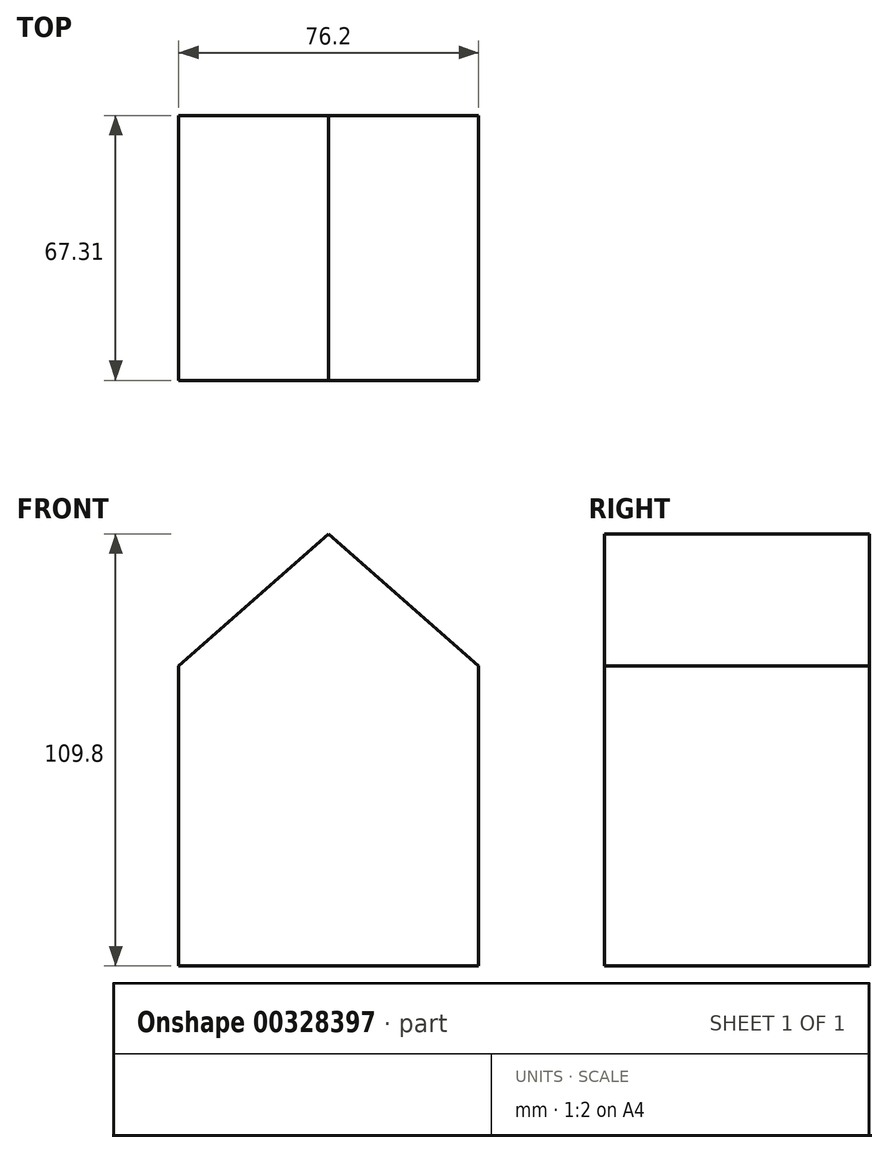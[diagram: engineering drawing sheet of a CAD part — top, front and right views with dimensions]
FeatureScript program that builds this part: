
annotation { "Feature Type Name" : "Feature", "Feature Type Description" : "" }
export const myFeature = defineFeature(function(context is Context, id is Id, definition is map)
    precondition{}
    {
        {
            var Q0;
            Q0=qCreatedBy(makeId("Front.planeOp"),FACE);
            var sketch = newSketch(context, id + "F0", { "sketchPlane" : qUnion([Q0])});
            skLineSegment(sketch, "E0.bottom", {"start": v(-38.1, 42.53) * mm, "end": v(38.1, 42.53) * mm});
            skLineSegment(sketch, "E0.top", {"start": v(-38.1, -33.67) * mm, "end": v(38.1, -33.67) * mm});
            skLineSegment(sketch, "E0.left", {"start": v(-38.1, 42.53) * mm, "end": v(-38.1, -33.67) * mm});
            skLineSegment(sketch, "E0.right", {"start": v(38.1, 42.53) * mm, "end": v(38.1, -33.67) * mm});
            skLineSegment(sketch, "E1", {"start": v(-38.1, 42.53) * mm, "end": v(0, 76.13) * mm});
            skLineSegment(sketch, "E2", {"start": v(0, 76.13) * mm, "end": v(38.1, 42.53) * mm});
            skSolve(sketch);
        }
        {
            var Q0;
            Q0=makeQuery(id+"F0.imprint","IMPRINT",FACE,{"disambiguationData":[TD([[makeQuery(id+"F0.imprint","IMPRINT",EDGE,{"derivedFrom":sQuery(id+"F0.wireOp",EDGE,"E0.bottom")}),1.0]])]});
            var Q1;
            Q1=makeQuery(id+"F0.imprint","IMPRINT",FACE,{"disambiguationData":[TD([[makeQuery(id+"F0.imprint","IMPRINT",EDGE,{"derivedFrom":sQuery(id+"F0.wireOp",EDGE,"E0.bottom")}),-1.0]])]});
            extrude(context, id + "F1", {"entities" : qUnion([Q0, Q1]), "depth" : 67.3 * mm, "offsetDistance" : 25.4 * mm});
        }
        {
            var Q0;
            Q0=makeQuery(id+"F1.opExtrude","CAP_FACE",FACE,{"disambiguationData":[OSD([sQuery(id+"F0.wireOp",EDGE,"E0.top"),sQuery(id+"F0.wireOp",EDGE,"E0.left"),sQuery(id+"F0.wireOp",EDGE,"E0.right"),sQuery(id+"F0.wireOp",EDGE,"E1"),sQuery(id+"F0.wireOp",EDGE,"E2")])],"isStart":false});
            var sketch = newSketch(context, id + "F2", { "sketchPlane" : qUnion([Q0])});
            skLineSegment(sketch, "E3.bottom", {"start": v(-6.35, -33.67) * mm, "end": v(6.35, -33.67) * mm});
            skLineSegment(sketch, "E3.top", {"start": v(-6.35, -8.27) * mm, "end": v(6.35, -8.27) * mm});
            skLineSegment(sketch, "E3.left", {"start": v(-6.35, -33.67) * mm, "end": v(-6.35, -8.27) * mm});
            skLineSegment(sketch, "E3.right", {"start": v(6.35, -33.67) * mm, "end": v(6.35, -8.27) * mm});
            skSolve(sketch);
        }
        {
            var Q0;
            Q0=makeQuery(id+"F2.imprint","IMPRINT",FACE,{"disambiguationData":[TD([[makeQuery(id+"F2.imprint","IMPRINT",EDGE,{"derivedFrom":sQuery(id+"F2.wireOp",EDGE,"E3.bottom")}),1.0]])]});
            extrude(context, id + "F3", {"entities" : qUnion([Q0]), "operationType" : NewBodyOperationType.ADD, "oppositeDirection" : true, "depth" : 10.92 * mm, "offsetDistance" : 25.4 * mm});
        }
    });
